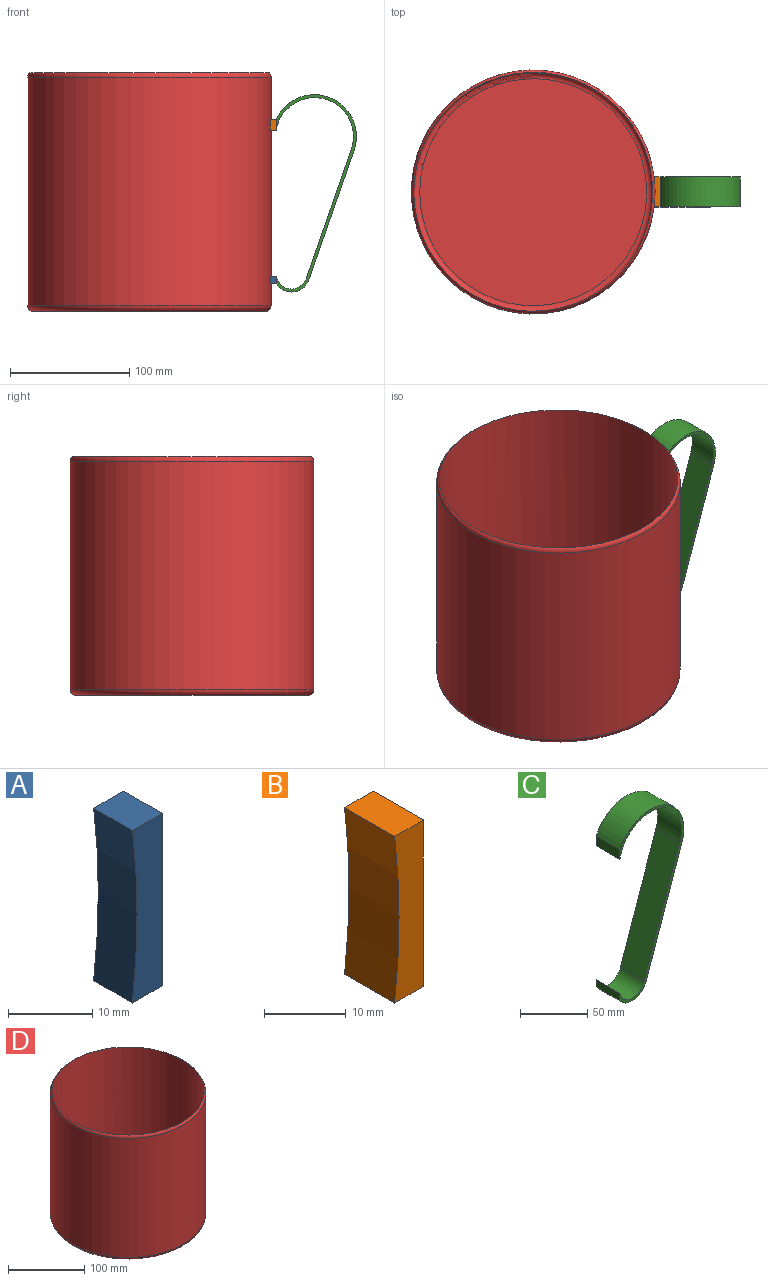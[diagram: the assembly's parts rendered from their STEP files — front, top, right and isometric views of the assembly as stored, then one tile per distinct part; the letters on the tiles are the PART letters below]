
ASSEMBLY  parts=4 mates=3
PART A: 6 faces, bbox 5x6.5x25 mm
  f0: plane 25x6.49mm, normal (1,0,0), area 162.2mm2, adj f1,f3,f4,f5
  f1: plane 6.49x5mm, normal (0,0,1), area 32.5mm2, adj f0,f2,f4,f5
  f2: cylinder r=102mm len=25mm, axis (0,1,0), area 162.7mm2, adj f1,f3,f4,f5
  f3: plane 6.49x5mm, normal (0,0,-1), area 32.5mm2, adj f0,f2,f4,f5
  f4: plane 25x5mm, normal (0,-1,0), area 112.2mm2, adj f0,f1,f2,f3
  f5: plane 25x5mm, normal (0,1,0), area 112.2mm2, adj f0,f1,f2,f3
PART B: 6 faces, bbox 5x8.7x25 mm
  f0: plane 25x8.68mm, normal (1,0,0), area 217mm2, adj f1,f3,f4,f5
  f1: plane 8.68x5mm, normal (0,0,1), area 43.4mm2, adj f0,f2,f4,f5
  f2: cylinder r=102mm len=25mm, axis (0,1,0), area 217.5mm2, adj f1,f3,f4,f5
  f3: plane 8.68x5mm, normal (0,0,-1), area 43.4mm2, adj f0,f2,f4,f5
  f4: plane 25x5mm, normal (0,-1,0), area 112.2mm2, adj f0,f1,f2,f3
  f5: plane 25x5mm, normal (0,1,0), area 112.2mm2, adj f0,f1,f2,f3
PART C: 10 faces, bbox 67.2x25x165.2 mm
  f0: cylinder r=32.59mm len=64.73mm, axis (0,1,0), area 2697.5mm2, adj f1,f7,f8,f9
  f1: plane 108.14x37.76mm, normal (-0.94,0,0.33), area 2863.6mm2, adj f0,f2,f8,f9
  f2: cylinder r=13.04mm len=25.15mm, axis (0,1,0), area 857.8mm2, adj f1,f3,f8,f9
  f3: plane 25x6.49mm, normal (-1,0,0), area 162.3mm2, adj f2,f4,f8,f9
  f4: cylinder r=15.54mm len=27.51mm, axis (0,1,0), area 857.6mm2, adj f3,f5,f8,f9
  f5: plane 108.14x37.76mm, normal (0.94,0,-0.33), area 2863.6mm2, adj f4,f6,f8,f9
  f6: cylinder r=35.09mm len=67.23mm, axis (0,1,0), area 2688.4mm2, adj f5,f7,f8,f9
  f7: plane 25x8.68mm, normal (-1,0,0), area 216.9mm2, adj f0,f6,f8,f9
  f8: plane 165.22x67.23mm, normal (0,-1,0), area 638.7mm2, adj f0,f1,f2,f3,f4,f5,f6,f7
  f9: plane 165.22x67.23mm, normal (0,1,0), area 638.7mm2, adj f0,f1,f2,f3,f4,f5,f6,f7
PART D: 7 faces, bbox 220.8x220.8x201 mm
  f0: plane 194x194mm, normal (0,0,-1), area 29559.2mm2, adj f4
  f1: plane 190x190mm, normal (0,0,1), area 28352.9mm2, adj f5
  f2: cylinder r=100mm len=200mm, axis (0,0,1), area 120637.2mm2, adj f5,f6
  f3: cylinder r=102mm len=204mm, axis (0,0,1), area 122409mm2, adj f4,f6
  f4: torus R=97mm, axis (0,0,1), area 4943.8mm2, adj f0,f3
  f5: torus R=95mm, axis (0,0,-1), area 4845.1mm2, adj f1,f2
  f6: torus R=97mm, axis (0,0,1), area 2951.5mm2, adj f2,f3
PLACE A rot(axis=(-1,0,0),90deg) t=(-62.08,61.61,80.39)mm
PLACE B rot(axis=(-1,0,0),90deg) t=(-62.08,61.61,209.14)mm
PLACE C t=(-53.42,74.11,166.65)mm
PLACE D rot(axis=(0,-1,0),0deg) t=(-165.81,61.61,197.18)mm
MATE fastened A.f0 <-> C.f3  axis (1,0,0) through (-59.58,61.61,83.64)mm
MATE fastened B.f0 <-> C.f7  axis (1,0,0) through (-59.58,61.61,213.48)mm
MATE revolute B.f2 <-> D.f2  axis (0,0,1) through (-165.81,61.61,217.82)mm
